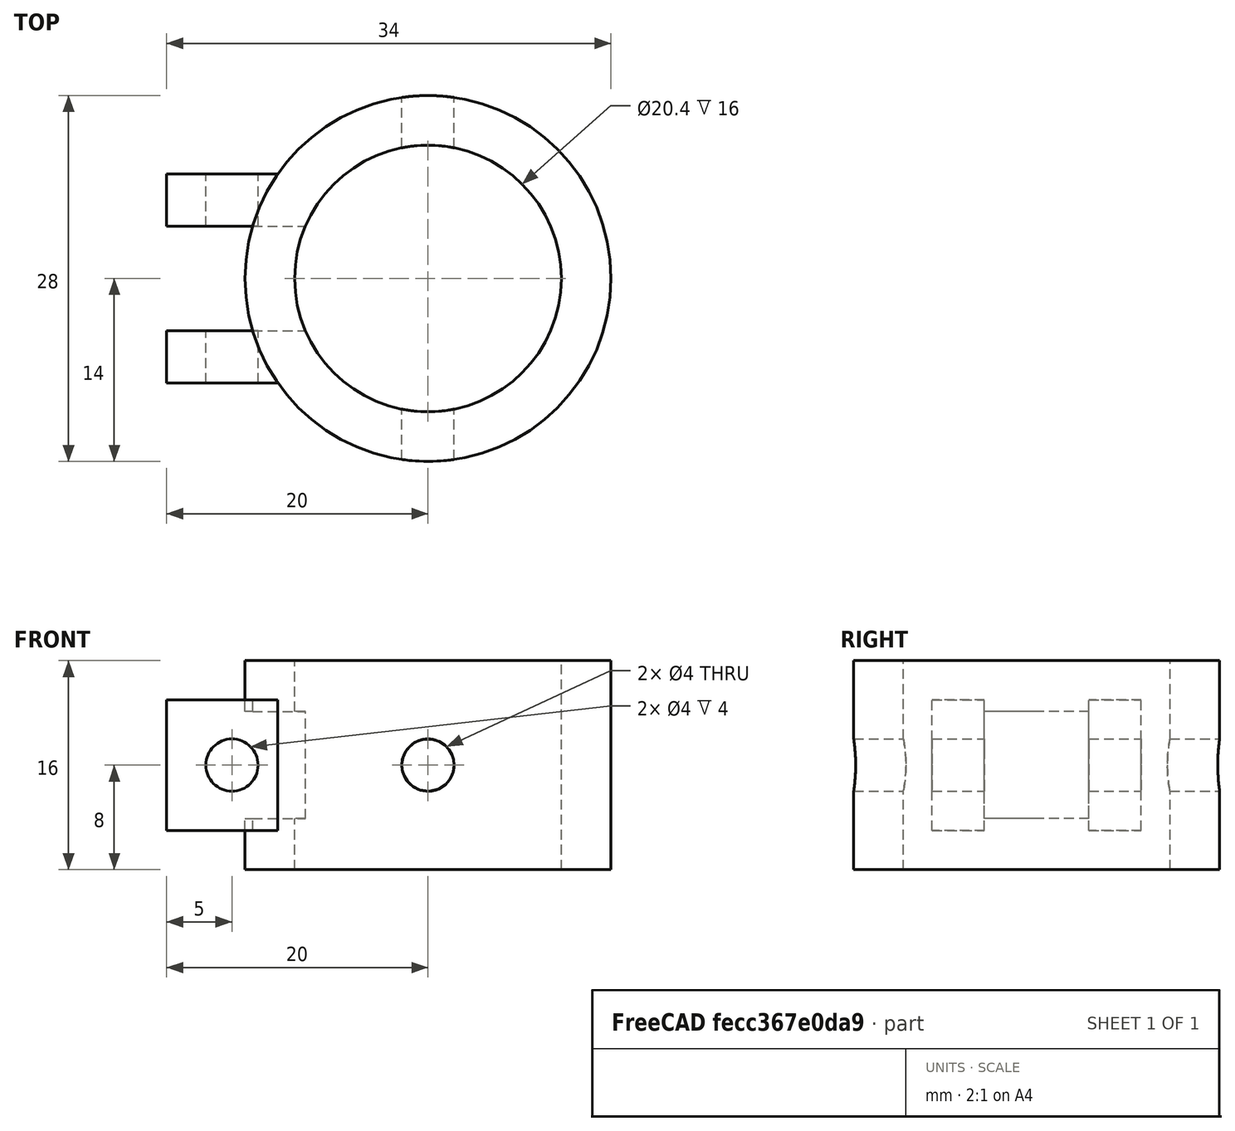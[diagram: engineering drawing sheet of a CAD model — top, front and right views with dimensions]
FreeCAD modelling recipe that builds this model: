
FCSTD DOCUMENT  (FreeCAD 0.17R13522 (Git))
Label: connector-rack
License: All rights reserved
LicenseURL: http://en.wikipedia.org/wiki/All_rights_reserved
objects: Part::Cylinder×4, Part::Box×3, Part::MultiFuse×2, Part::Cut×1
note: 10 computed .brp shape members not serialized (recipe doc carries the construction recipe); baked Part::Feature solids carry a one-line shape summary decoded from their .brp

FEATURE [Part::Cylinder] Cylinder002
  Angle = 360
  AttacherType = Attacher::AttachEngine3D
  Height = 28
  Placement = pos=(-10,0,-10) rot=(0,0,1;0rad)
  Radius = 10.2
FEATURE [Part::Box] Box  label="Cube"
  AttacherType = Attacher::AttachEngine3D
  Height = 10
  Length = 10
  Placement = pos=(-30,-8,-5) rot=(0,0,1;0rad)
  Width = 4
FEATURE [Part::Cylinder] Cylinder004
  Angle = 360
  AttacherType = Attacher::AttachEngine3D
  Height = 16
  Placement = pos=(-25,-8,0) rot=(-1,0,0;1.5708rad)
  Radius = 2
FEATURE [Part::Cylinder] Cylinder
  Angle = 360
  AttacherType = Attacher::AttachEngine3D
  Height = 16
  Placement = pos=(-10,0,-8) rot=(0,0,1;0rad)
  Radius = 14
FEATURE [Part::Box] Box001  label="Cube001"
  AttacherType = Attacher::AttachEngine3D
  Height = 8.2
  Length = 5
  Placement = pos=(-24,-4,-4.1) rot=(0,0,1;0rad)
  Width = 8
FEATURE [Part::Cylinder] Cylinder006
  Angle = 360
  AttacherType = Attacher::AttachEngine3D
  Height = 30
  Placement = pos=(-10,-15,0) rot=(-1,0,0;1.5708rad)
  Radius = 2
FEATURE [Part::MultiFuse] Fusion001  label="Negative Fusion"
  Shapes = -> [Cylinder002,Cylinder004,Box001,Cylinder006]
FEATURE [Part::Box] Box002  label="Cube002"
  AttacherType = Attacher::AttachEngine3D
  Height = 10
  Length = 10
  Placement = pos=(-30,4,-5) rot=(0,0,1;0rad)
  Width = 4
FEATURE [Part::MultiFuse] Fusion  label="Positive Fusion"
  Shapes = -> [Cylinder,Box,Box002]
FEATURE [Part::Cut] Cut
  Base = -> Fusion
  Tool = -> Fusion001
